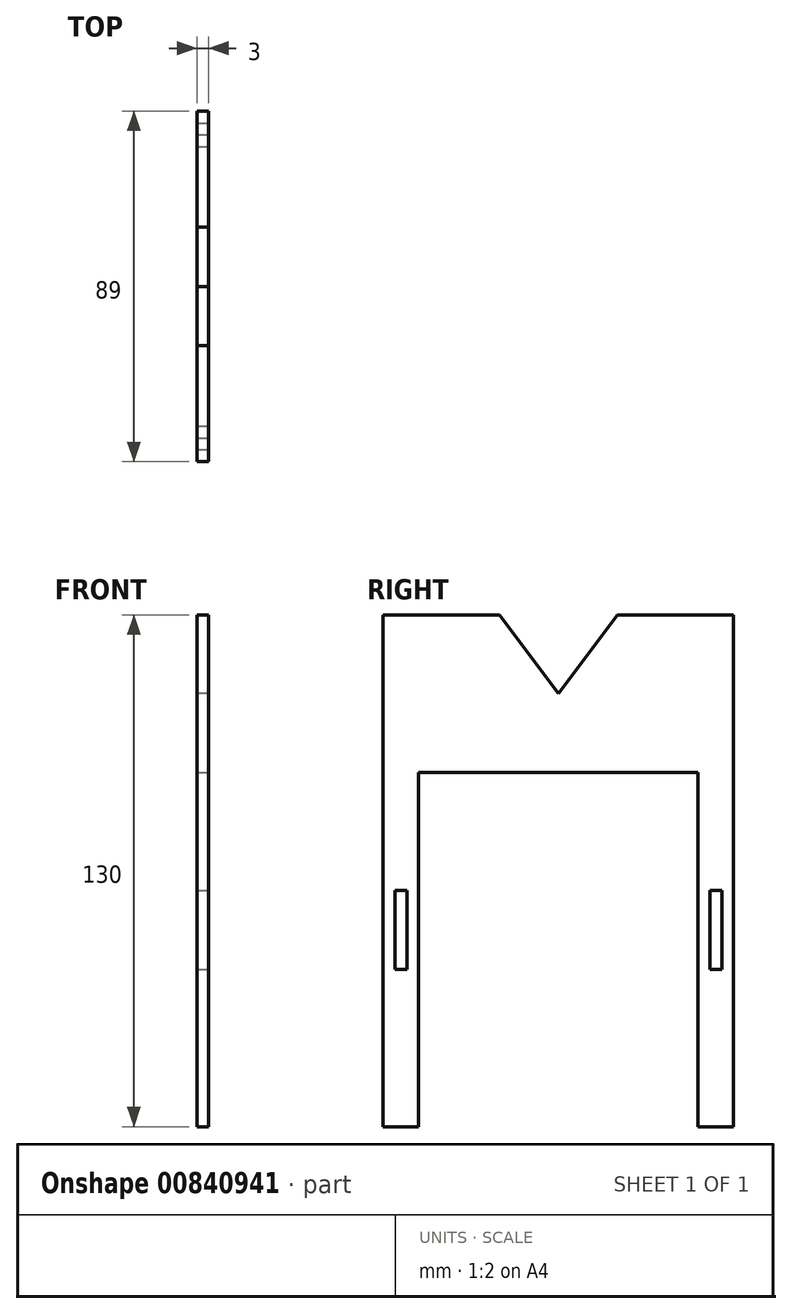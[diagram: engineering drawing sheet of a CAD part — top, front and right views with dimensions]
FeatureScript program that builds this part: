
annotation { "Feature Type Name" : "Feature", "Feature Type Description" : "" }
export const myFeature = defineFeature(function(context is Context, id is Id, definition is map)
    precondition{}
    {
        {
            var Q0;
            Q0=qCreatedBy(makeId("Right.planeOp"),FACE);
            var sketch = newSketch(context, id + "F0", { "sketchPlane" : qUnion([Q0])});
            skLineSegment(sketch, "E0", {"start": v(0, 130) * mm, "end": v(29.5, 130) * mm});
            skLineSegment(sketch, "E1", {"start": v(29.5, 130) * mm, "end": v(44.5, 110) * mm});
            skLineSegment(sketch, "E2", {"start": v(44.5, 110) * mm, "end": v(59.5, 130) * mm});
            skLineSegment(sketch, "E3", {"start": v(59.5, 130) * mm, "end": v(89, 130) * mm});
            skLineSegment(sketch, "E4", {"start": v(89, 130) * mm, "end": v(89, 0) * mm});
            skLineSegment(sketch, "E5", {"start": v(89, 0) * mm, "end": v(0, 0) * mm});
            skLineSegment(sketch, "E6", {"start": v(0, 0) * mm, "end": v(0, 130) * mm});
            skSolve(sketch);
        }
        {
            var Q0;
            Q0=qSketchRegion(id+"F0",true);
            extrude(context, id + "F1", {"entities" : qUnion([Q0]), "depth" : 3 * mm, "offsetDistance" : 25 * mm});
        }
        {
            var Q0;
            Q0=makeQuery(id+"F1.opExtrude","CAP_FACE",FACE,{"disambiguationData":[OSD([sQuery(id+"F0.wireOp",EDGE,"E0"),sQuery(id+"F0.wireOp",EDGE,"E1"),sQuery(id+"F0.wireOp",EDGE,"E2"),sQuery(id+"F0.wireOp",EDGE,"E3"),sQuery(id+"F0.wireOp",EDGE,"E4"),sQuery(id+"F0.wireOp",EDGE,"E5"),sQuery(id+"F0.wireOp",EDGE,"E6")])],"isStart":false});
            var sketch = newSketch(context, id + "F2", { "sketchPlane" : qUnion([Q0])});
            skLineSegment(sketch, "E7.bottom", {"start": v(3, 60) * mm, "end": v(6, 60) * mm});
            skLineSegment(sketch, "E7.top", {"start": v(3, 40) * mm, "end": v(6, 40) * mm});
            skLineSegment(sketch, "E7.left", {"start": v(3, 60) * mm, "end": v(3, 40) * mm});
            skLineSegment(sketch, "E7.right", {"start": v(6, 60) * mm, "end": v(6, 40) * mm});
            skLineSegment(sketch, "E8", {"start": v(44.5, 110) * mm, "end": v(44.5, 73.4) * mm, "construction": true});
            skLineSegment(sketch, "E9.MirrorCS", {"start": v(83, 60) * mm, "end": v(83, 40) * mm});
            skLineSegment(sketch, "E10.MirrorCS", {"start": v(86, 60) * mm, "end": v(83, 60) * mm});
            skLineSegment(sketch, "E11.MirrorCS", {"start": v(86, 40) * mm, "end": v(83, 40) * mm});
            skLineSegment(sketch, "E12.MirrorCS", {"start": v(86, 60) * mm, "end": v(86, 40) * mm});
            skLineSegment(sketch, "E13.bottom", {"start": v(9, 0) * mm, "end": v(80, 0) * mm});
            skLineSegment(sketch, "E13.top", {"start": v(9, 90) * mm, "end": v(80, 90) * mm});
            skLineSegment(sketch, "E13.left", {"start": v(9, 0) * mm, "end": v(9, 90) * mm});
            skLineSegment(sketch, "E13.right", {"start": v(80, 0) * mm, "end": v(80, 90) * mm});
            skSolve(sketch);
        }
        {
            var Q0;
            Q0=qSketchRegion(id+"F2",true);
            extrude(context, id + "F3", {"entities" : qUnion([Q0]), "operationType" : NewBodyOperationType.REMOVE, "oppositeDirection" : true, "depth" : 25 * mm, "offsetDistance" : 25 * mm});
        }
    });
